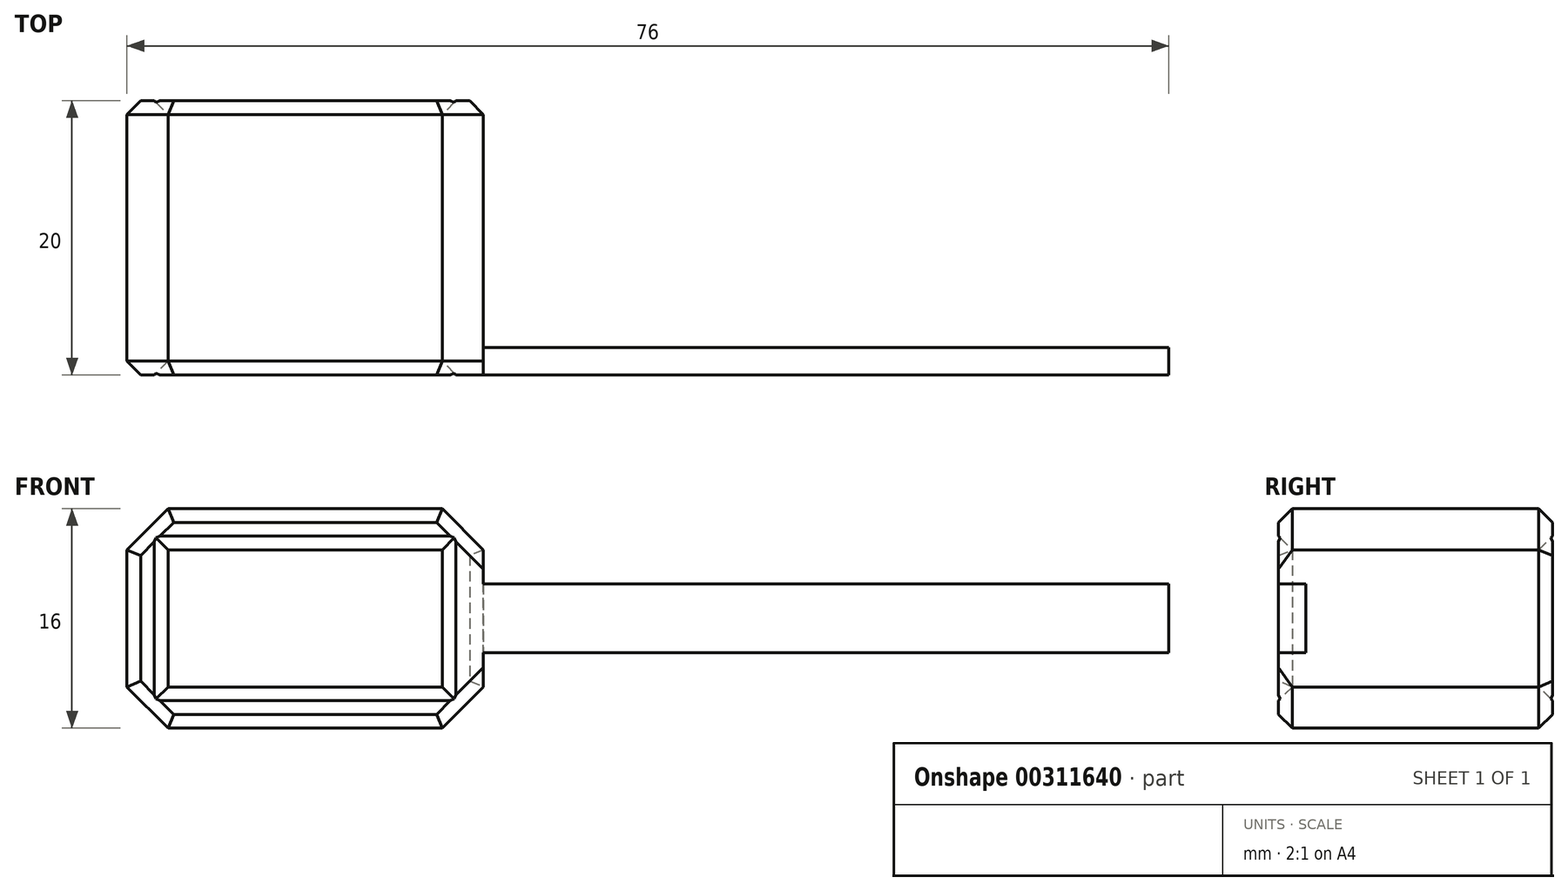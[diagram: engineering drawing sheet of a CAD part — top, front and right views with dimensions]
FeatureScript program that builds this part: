
annotation { "Feature Type Name" : "Feature", "Feature Type Description" : "" }
export const myFeature = defineFeature(function(context is Context, id is Id, definition is map)
    precondition{}
    {
        {
            var Q0;
            Q0=qCreatedBy(makeId("Front.planeOp"),FACE);
            var sketch = newSketch(context, id + "F0", { "sketchPlane" : qUnion([Q0])});
            skLineSegment(sketch, "E0", {"start": v(0, 0) * mm, "end": v(0, 10) * mm});
            skLineSegment(sketch, "E1", {"start": v(0, 10) * mm, "end": v(20, 10) * mm});
            skLineSegment(sketch, "E2", {"start": v(20, 10) * mm, "end": v(20, 0) * mm});
            skLineSegment(sketch, "E3", {"start": v(20, 0) * mm, "end": v(0, 0) * mm});
            skLineSegment(sketch, "E4", {"start": v(-3, 13) * mm, "end": v(23, 13) * mm});
            skLineSegment(sketch, "E5", {"start": v(23, 13) * mm, "end": v(23, -3) * mm});
            skLineSegment(sketch, "E6", {"start": v(23, -3) * mm, "end": v(-3, -3) * mm});
            skLineSegment(sketch, "E7", {"start": v(-3, -3) * mm, "end": v(-3, 13) * mm});
            skLineSegment(sketch, "E8", {"start": v(20, 10) * mm, "end": v(23, 10) * mm, "construction": true});
            skLineSegment(sketch, "E9", {"start": v(0, 10) * mm, "end": v(-3, 10) * mm, "construction": true});
            skLineSegment(sketch, "E10", {"start": v(0, 10) * mm, "end": v(0, 13) * mm, "construction": true});
            skLineSegment(sketch, "E11", {"start": v(0, 0) * mm, "end": v(0, -3) * mm, "construction": true});
            skSolve(sketch);
        }
        {
            var Q0;
            Q0=makeQuery(id+"F0.imprint","IMPRINT",FACE,{"disambiguationData":[TD([[makeQuery(id+"F0.imprint","IMPRINT",EDGE,{"derivedFrom":sQuery(id+"F0.wireOp",EDGE,"E0")}),1.0]])]});
            extrude(context, id + "F1", {"entities" : qUnion([Q0]), "depth" : 20 * mm});
        }
        {
            var Q0;
            Q0=makeQuery(id+"F1.opExtrude","SWEPT_FACE",FACE,{"disambiguationData":[OSD([sQuery(id+"F0.wireOp",EDGE,"E5")])]});
            var sketch = newSketch(context, id + "F2", { "sketchPlane" : qUnion([Q0])});
            skLineSegment(sketch, "E12", {"start": v(-20, 5) * mm, "end": v(-18, 5) * mm, "construction": true});
            skPoint(sketch, "E12.endSnap0", {"position": v(-20, 5) * mm});
            skLineSegment(sketch, "E13", {"start": v(-18, 5) * mm, "end": v(-18, 2.5) * mm});
            skLineSegment(sketch, "E14", {"start": v(-18, 2.5) * mm, "end": v(-20, 2.5) * mm});
            skLineSegment(sketch, "E15", {"start": v(-20, 2.5) * mm, "end": v(-20, 5) * mm});
            skLineSegment(sketch, "E16", {"start": v(-20, 5) * mm, "end": v(-20, 7.5) * mm});
            skLineSegment(sketch, "E17", {"start": v(-20, 7.5) * mm, "end": v(-18, 7.5) * mm});
            skLineSegment(sketch, "E18", {"start": v(-18, 7.5) * mm, "end": v(-18, 5) * mm});
            skSolve(sketch);
        }
        {
            var Q0;
            Q0 = qSketchRegion(id + "F2", true);
            extrude(context, id + "F3", {"entities" : qUnion([Q0]), "operationType" : NewBodyOperationType.ADD, "depth" : 50 * mm});
        }
        {
            var Q0;
            Q0=makeQuery(id+"F1.opExtrude","SWEPT_EDGE",EDGE,{"disambiguationData":[OSD([sQuery(id+"F0.wireOp",EDGE,"E4"),sQuery(id+"F0.wireOp",EDGE,"E7")])]});
            var Q1;
            Q1=makeQuery(id+"F1.opExtrude","SWEPT_EDGE",EDGE,{"disambiguationData":[OSD([sQuery(id+"F0.wireOp",EDGE,"E4"),sQuery(id+"F0.wireOp",EDGE,"E5")])]});
            var Q2;
            Q2=makeQuery(id+"F3.opExtrude","CAP_EDGE",EDGE,{"disambiguationData":[OSD([sQuery(id+"F2.wireOp",EDGE,"E13"),sQuery(id+"F2.wireOp",EDGE,"E18")])],"isStart":true});
            var Q3;
            Q3=makeQuery(id+"F1.opExtrude","SWEPT_EDGE",EDGE,{"disambiguationData":[OSD([sQuery(id+"F0.wireOp",EDGE,"E6"),sQuery(id+"F0.wireOp",EDGE,"E7")])]});
            var Q4;
            Q4=makeQuery(id+"F1.opExtrude","SWEPT_EDGE",EDGE,{"disambiguationData":[OSD([sQuery(id+"F0.wireOp",EDGE,"E5"),sQuery(id+"F0.wireOp",EDGE,"E6")])]});
            chamfer(context, id + "F4", {"entities" : qUnion([Q0, Q1, Q2, Q3, Q4]), "width" : 3 * mm, "tangentPropagation" : true});
        }
        {
            var Q0;
            Q0=makeQuery(id+"F1.opExtrude","CAP_EDGE",EDGE,{"disambiguationData":[OSD([sQuery(id+"F0.wireOp",EDGE,"E2")])],"isStart":true});
            var Q1;
            Q1=makeQuery(id+"F1.opExtrude","CAP_EDGE",EDGE,{"disambiguationData":[OSD([sQuery(id+"F0.wireOp",EDGE,"E1")])],"isStart":true});
            var Q2;
            Q2=makeQuery(id+"F1.opExtrude","CAP_EDGE",EDGE,{"disambiguationData":[OSD([sQuery(id+"F0.wireOp",EDGE,"E3")])],"isStart":true});
            var Q3;
            Q3=makeQuery(id+"F1.opExtrude","CAP_EDGE",EDGE,{"disambiguationData":[OSD([sQuery(id+"F0.wireOp",EDGE,"E0")])],"isStart":true});
            var Q4;
            {var subQ0=sQuery(id+"F0.wireOp",EDGE,"E7");var subQ1=sQuery(id+"F0.wireOp",EDGE,"E6");Q4=makeQuery(id+"F4.opChamfer","BLEND_EDGE",EDGE,{"blendedFrom":[makeQuery(id+"F1.opExtrude","SWEPT_EDGE",EDGE,{"disambiguationData":[OSD([subQ1,subQ0])]}),makeQuery(id+"F1.opExtrude","CAP_FACE",FACE,{"disambiguationData":[OSD([sQuery(id+"F0.wireOp",EDGE,"E0"),sQuery(id+"F0.wireOp",EDGE,"E1"),sQuery(id+"F0.wireOp",EDGE,"E2"),sQuery(id+"F0.wireOp",EDGE,"E3"),sQuery(id+"F0.wireOp",EDGE,"E4"),sQuery(id+"F0.wireOp",EDGE,"E5"),subQ1,subQ0])],"isStart":true})],"blendedInto":[makeQuery(id+"F1.opExtrude","CAP_FACE",FACE,{"disambiguationData":[OSD([sQuery(id+"F0.wireOp",EDGE,"E0"),sQuery(id+"F0.wireOp",EDGE,"E1"),sQuery(id+"F0.wireOp",EDGE,"E2"),sQuery(id+"F0.wireOp",EDGE,"E3"),sQuery(id+"F0.wireOp",EDGE,"E4"),sQuery(id+"F0.wireOp",EDGE,"E5"),subQ1,subQ0])],"isStart":true})]});}
            var Q5;
            {var subQ0=sQuery(id+"F0.wireOp",EDGE,"E6");var subQ1=sQuery(id+"F0.wireOp",EDGE,"E5");Q5=makeQuery(id+"F4.opChamfer","BLEND_EDGE",EDGE,{"blendedFrom":[makeQuery(id+"F1.opExtrude","SWEPT_EDGE",EDGE,{"disambiguationData":[OSD([subQ1,subQ0])]}),makeQuery(id+"F1.opExtrude","CAP_FACE",FACE,{"disambiguationData":[OSD([sQuery(id+"F0.wireOp",EDGE,"E0"),sQuery(id+"F0.wireOp",EDGE,"E1"),sQuery(id+"F0.wireOp",EDGE,"E2"),sQuery(id+"F0.wireOp",EDGE,"E3"),sQuery(id+"F0.wireOp",EDGE,"E4"),subQ1,subQ0,sQuery(id+"F0.wireOp",EDGE,"E7")])],"isStart":true})],"blendedInto":[makeQuery(id+"F1.opExtrude","CAP_FACE",FACE,{"disambiguationData":[OSD([sQuery(id+"F0.wireOp",EDGE,"E0"),sQuery(id+"F0.wireOp",EDGE,"E1"),sQuery(id+"F0.wireOp",EDGE,"E2"),sQuery(id+"F0.wireOp",EDGE,"E3"),sQuery(id+"F0.wireOp",EDGE,"E4"),subQ1,subQ0,sQuery(id+"F0.wireOp",EDGE,"E7")])],"isStart":true})]});}
            var Q6;
            {var subQ0=sQuery(id+"F0.wireOp",EDGE,"E5");var subQ1=sQuery(id+"F0.wireOp",EDGE,"E4");Q6=makeQuery(id+"F4.opChamfer","BLEND_EDGE",EDGE,{"blendedFrom":[makeQuery(id+"F1.opExtrude","SWEPT_EDGE",EDGE,{"disambiguationData":[OSD([subQ1,subQ0])]}),makeQuery(id+"F1.opExtrude","CAP_FACE",FACE,{"disambiguationData":[OSD([sQuery(id+"F0.wireOp",EDGE,"E0"),sQuery(id+"F0.wireOp",EDGE,"E1"),sQuery(id+"F0.wireOp",EDGE,"E2"),sQuery(id+"F0.wireOp",EDGE,"E3"),subQ1,subQ0,sQuery(id+"F0.wireOp",EDGE,"E6"),sQuery(id+"F0.wireOp",EDGE,"E7")])],"isStart":true})],"blendedInto":[makeQuery(id+"F1.opExtrude","CAP_FACE",FACE,{"disambiguationData":[OSD([sQuery(id+"F0.wireOp",EDGE,"E0"),sQuery(id+"F0.wireOp",EDGE,"E1"),sQuery(id+"F0.wireOp",EDGE,"E2"),sQuery(id+"F0.wireOp",EDGE,"E3"),subQ1,subQ0,sQuery(id+"F0.wireOp",EDGE,"E6"),sQuery(id+"F0.wireOp",EDGE,"E7")])],"isStart":true})]});}
            var Q7;
            {var subQ0=sQuery(id+"F0.wireOp",EDGE,"E7");var subQ1=sQuery(id+"F0.wireOp",EDGE,"E4");Q7=makeQuery(id+"F4.opChamfer","BLEND_EDGE",EDGE,{"blendedFrom":[makeQuery(id+"F1.opExtrude","SWEPT_EDGE",EDGE,{"disambiguationData":[OSD([subQ1,subQ0])]}),makeQuery(id+"F1.opExtrude","CAP_FACE",FACE,{"disambiguationData":[OSD([sQuery(id+"F0.wireOp",EDGE,"E0"),sQuery(id+"F0.wireOp",EDGE,"E1"),sQuery(id+"F0.wireOp",EDGE,"E2"),sQuery(id+"F0.wireOp",EDGE,"E3"),subQ1,sQuery(id+"F0.wireOp",EDGE,"E5"),sQuery(id+"F0.wireOp",EDGE,"E6"),subQ0])],"isStart":true})],"blendedInto":[makeQuery(id+"F1.opExtrude","CAP_FACE",FACE,{"disambiguationData":[OSD([sQuery(id+"F0.wireOp",EDGE,"E0"),sQuery(id+"F0.wireOp",EDGE,"E1"),sQuery(id+"F0.wireOp",EDGE,"E2"),sQuery(id+"F0.wireOp",EDGE,"E3"),subQ1,sQuery(id+"F0.wireOp",EDGE,"E5"),sQuery(id+"F0.wireOp",EDGE,"E6"),subQ0])],"isStart":true})]});}
            var Q8;
            Q8=makeQuery(id+"F1.opExtrude","CAP_EDGE",EDGE,{"disambiguationData":[OSD([sQuery(id+"F0.wireOp",EDGE,"E6")])],"isStart":true});
            var Q9;
            Q9=makeQuery(id+"F1.opExtrude","CAP_EDGE",EDGE,{"disambiguationData":[OSD([sQuery(id+"F0.wireOp",EDGE,"E5")])],"isStart":true});
            var Q10;
            Q10=makeQuery(id+"F1.opExtrude","CAP_EDGE",EDGE,{"disambiguationData":[OSD([sQuery(id+"F0.wireOp",EDGE,"E4")])],"isStart":true});
            var Q11;
            Q11=makeQuery(id+"F1.opExtrude","CAP_EDGE",EDGE,{"disambiguationData":[OSD([sQuery(id+"F0.wireOp",EDGE,"E7")])],"isStart":true});
            chamfer(context, id + "F5", {"entities" : qUnion([Q0, Q1, Q2, Q3, Q4, Q5, Q6, Q7, Q8, Q9, Q10, Q11]), "width" : 1 * mm, "tangentPropagation" : true});
        }
        {
            var Q0;
            {var subQ0=sQuery(id+"F0.wireOp",EDGE,"E7");var subQ1=sQuery(id+"F0.wireOp",EDGE,"E6");Q0=makeQuery(id+"F4.opChamfer","BLEND_EDGE",EDGE,{"blendedFrom":[makeQuery(id+"F1.opExtrude","SWEPT_EDGE",EDGE,{"disambiguationData":[OSD([subQ1,subQ0])]}),makeQuery(id+"F3.boolean.opBoolean","MERGE",FACE,{"derivedFrom":[makeQuery(id+"F1.opExtrude","CAP_FACE",FACE,{"disambiguationData":[OSD([sQuery(id+"F0.wireOp",EDGE,"E0"),sQuery(id+"F0.wireOp",EDGE,"E1"),sQuery(id+"F0.wireOp",EDGE,"E2"),sQuery(id+"F0.wireOp",EDGE,"E3"),sQuery(id+"F0.wireOp",EDGE,"E4"),sQuery(id+"F0.wireOp",EDGE,"E5"),subQ1,subQ0])],"isStart":false}),makeQuery(id+"F3.opExtrude","SWEPT_FACE",FACE,{"disambiguationData":[OSD([sQuery(id+"F2.wireOp",EDGE,"E15"),sQuery(id+"F2.wireOp",EDGE,"E16")])]})]})],"blendedInto":[makeQuery(id+"F3.boolean.opBoolean","MERGE",FACE,{"derivedFrom":[makeQuery(id+"F1.opExtrude","CAP_FACE",FACE,{"disambiguationData":[OSD([sQuery(id+"F0.wireOp",EDGE,"E0"),sQuery(id+"F0.wireOp",EDGE,"E1"),sQuery(id+"F0.wireOp",EDGE,"E2"),sQuery(id+"F0.wireOp",EDGE,"E3"),sQuery(id+"F0.wireOp",EDGE,"E4"),sQuery(id+"F0.wireOp",EDGE,"E5"),subQ1,subQ0])],"isStart":false}),makeQuery(id+"F3.opExtrude","SWEPT_FACE",FACE,{"disambiguationData":[OSD([sQuery(id+"F2.wireOp",EDGE,"E15"),sQuery(id+"F2.wireOp",EDGE,"E16")])]})]})]});}
            var Q1;
            Q1=makeQuery(id+"F1.opExtrude","CAP_EDGE",EDGE,{"disambiguationData":[OSD([sQuery(id+"F0.wireOp",EDGE,"E0")])],"isStart":false});
            var Q2;
            {var subQ0=sQuery(id+"F0.wireOp",EDGE,"E7");var subQ1=sQuery(id+"F0.wireOp",EDGE,"E4");Q2=makeQuery(id+"F4.opChamfer","BLEND_EDGE",EDGE,{"blendedFrom":[makeQuery(id+"F1.opExtrude","SWEPT_EDGE",EDGE,{"disambiguationData":[OSD([subQ1,subQ0])]}),makeQuery(id+"F3.boolean.opBoolean","MERGE",FACE,{"derivedFrom":[makeQuery(id+"F1.opExtrude","CAP_FACE",FACE,{"disambiguationData":[OSD([sQuery(id+"F0.wireOp",EDGE,"E0"),sQuery(id+"F0.wireOp",EDGE,"E1"),sQuery(id+"F0.wireOp",EDGE,"E2"),sQuery(id+"F0.wireOp",EDGE,"E3"),subQ1,sQuery(id+"F0.wireOp",EDGE,"E5"),sQuery(id+"F0.wireOp",EDGE,"E6"),subQ0])],"isStart":false}),makeQuery(id+"F3.opExtrude","SWEPT_FACE",FACE,{"disambiguationData":[OSD([sQuery(id+"F2.wireOp",EDGE,"E15"),sQuery(id+"F2.wireOp",EDGE,"E16")])]})]})],"blendedInto":[makeQuery(id+"F3.boolean.opBoolean","MERGE",FACE,{"derivedFrom":[makeQuery(id+"F1.opExtrude","CAP_FACE",FACE,{"disambiguationData":[OSD([sQuery(id+"F0.wireOp",EDGE,"E0"),sQuery(id+"F0.wireOp",EDGE,"E1"),sQuery(id+"F0.wireOp",EDGE,"E2"),sQuery(id+"F0.wireOp",EDGE,"E3"),subQ1,sQuery(id+"F0.wireOp",EDGE,"E5"),sQuery(id+"F0.wireOp",EDGE,"E6"),subQ0])],"isStart":false}),makeQuery(id+"F3.opExtrude","SWEPT_FACE",FACE,{"disambiguationData":[OSD([sQuery(id+"F2.wireOp",EDGE,"E15"),sQuery(id+"F2.wireOp",EDGE,"E16")])]})]})]});}
            var Q3;
            {var subQ0=sQuery(id+"F0.wireOp",EDGE,"E5");var subQ1=sQuery(id+"F0.wireOp",EDGE,"E4");Q3=makeQuery(id+"F4.opChamfer","BLEND_EDGE",EDGE,{"blendedFrom":[makeQuery(id+"F1.opExtrude","SWEPT_EDGE",EDGE,{"disambiguationData":[OSD([subQ1,subQ0])]}),makeQuery(id+"F3.boolean.opBoolean","MERGE",FACE,{"derivedFrom":[makeQuery(id+"F1.opExtrude","CAP_FACE",FACE,{"disambiguationData":[OSD([sQuery(id+"F0.wireOp",EDGE,"E0"),sQuery(id+"F0.wireOp",EDGE,"E1"),sQuery(id+"F0.wireOp",EDGE,"E2"),sQuery(id+"F0.wireOp",EDGE,"E3"),subQ1,subQ0,sQuery(id+"F0.wireOp",EDGE,"E6"),sQuery(id+"F0.wireOp",EDGE,"E7")])],"isStart":false}),makeQuery(id+"F3.opExtrude","SWEPT_FACE",FACE,{"disambiguationData":[OSD([sQuery(id+"F2.wireOp",EDGE,"E15"),sQuery(id+"F2.wireOp",EDGE,"E16")])]})]})],"blendedInto":[makeQuery(id+"F3.boolean.opBoolean","MERGE",FACE,{"derivedFrom":[makeQuery(id+"F1.opExtrude","CAP_FACE",FACE,{"disambiguationData":[OSD([sQuery(id+"F0.wireOp",EDGE,"E0"),sQuery(id+"F0.wireOp",EDGE,"E1"),sQuery(id+"F0.wireOp",EDGE,"E2"),sQuery(id+"F0.wireOp",EDGE,"E3"),subQ1,subQ0,sQuery(id+"F0.wireOp",EDGE,"E6"),sQuery(id+"F0.wireOp",EDGE,"E7")])],"isStart":false}),makeQuery(id+"F3.opExtrude","SWEPT_FACE",FACE,{"disambiguationData":[OSD([sQuery(id+"F2.wireOp",EDGE,"E15"),sQuery(id+"F2.wireOp",EDGE,"E16")])]})]})]});}
            var Q4;
            {var subQ0=sQuery(id+"F0.wireOp",EDGE,"E6");var subQ1=sQuery(id+"F0.wireOp",EDGE,"E5");Q4=makeQuery(id+"F4.opChamfer","BLEND_EDGE",EDGE,{"blendedFrom":[makeQuery(id+"F1.opExtrude","SWEPT_EDGE",EDGE,{"disambiguationData":[OSD([subQ1,subQ0])]}),makeQuery(id+"F3.boolean.opBoolean","MERGE",FACE,{"derivedFrom":[makeQuery(id+"F1.opExtrude","CAP_FACE",FACE,{"disambiguationData":[OSD([sQuery(id+"F0.wireOp",EDGE,"E0"),sQuery(id+"F0.wireOp",EDGE,"E1"),sQuery(id+"F0.wireOp",EDGE,"E2"),sQuery(id+"F0.wireOp",EDGE,"E3"),sQuery(id+"F0.wireOp",EDGE,"E4"),subQ1,subQ0,sQuery(id+"F0.wireOp",EDGE,"E7")])],"isStart":false}),makeQuery(id+"F3.opExtrude","SWEPT_FACE",FACE,{"disambiguationData":[OSD([sQuery(id+"F2.wireOp",EDGE,"E15"),sQuery(id+"F2.wireOp",EDGE,"E16")])]})]})],"blendedInto":[makeQuery(id+"F3.boolean.opBoolean","MERGE",FACE,{"derivedFrom":[makeQuery(id+"F1.opExtrude","CAP_FACE",FACE,{"disambiguationData":[OSD([sQuery(id+"F0.wireOp",EDGE,"E0"),sQuery(id+"F0.wireOp",EDGE,"E1"),sQuery(id+"F0.wireOp",EDGE,"E2"),sQuery(id+"F0.wireOp",EDGE,"E3"),sQuery(id+"F0.wireOp",EDGE,"E4"),subQ1,subQ0,sQuery(id+"F0.wireOp",EDGE,"E7")])],"isStart":false}),makeQuery(id+"F3.opExtrude","SWEPT_FACE",FACE,{"disambiguationData":[OSD([sQuery(id+"F2.wireOp",EDGE,"E15"),sQuery(id+"F2.wireOp",EDGE,"E16")])]})]})]});}
            var Q5;
            Q5=makeQuery(id+"F1.opExtrude","CAP_EDGE",EDGE,{"disambiguationData":[OSD([sQuery(id+"F0.wireOp",EDGE,"E6")])],"isStart":false});
            var Q6;
            Q6=makeQuery(id+"F1.opExtrude","CAP_EDGE",EDGE,{"disambiguationData":[OSD([sQuery(id+"F0.wireOp",EDGE,"E4")])],"isStart":false});
            var Q7;
            Q7=makeQuery(id+"F1.opExtrude","CAP_EDGE",EDGE,{"disambiguationData":[OSD([sQuery(id+"F0.wireOp",EDGE,"E3")])],"isStart":false});
            var Q8;
            Q8=makeQuery(id+"F1.opExtrude","CAP_EDGE",EDGE,{"disambiguationData":[OSD([sQuery(id+"F0.wireOp",EDGE,"E1")])],"isStart":false});
            var Q9;
            Q9=makeQuery(id+"F1.opExtrude","CAP_EDGE",EDGE,{"disambiguationData":[OSD([sQuery(id+"F0.wireOp",EDGE,"E2")])],"isStart":false});
            chamfer(context, id + "F6", {"entities" : qUnion([Q0, Q1, Q2, Q3, Q4, Q5, Q6, Q7, Q8, Q9]), "width" : 1 * mm, "tangentPropagation" : true});
        }
        {
            var Q0;
            Q0=makeQuery(id+"F1.opExtrude","CAP_EDGE",EDGE,{"disambiguationData":[OSD([sQuery(id+"F0.wireOp",EDGE,"E7")])],"isStart":false});
            chamfer(context, id + "F7", {"entities" : qUnion([Q0]), "width" : 1 * mm, "tangentPropagation" : true});
        }
    });
